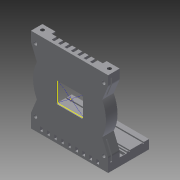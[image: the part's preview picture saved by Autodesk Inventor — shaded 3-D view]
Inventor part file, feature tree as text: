
AUTODESK INVENTOR PART (.ipt)
format: ipt  version: 2013 (Build 170138000, 138)  size: 804,864 bytes
history: native  units: in
note: dims shown in document units (in); Inventor stores cm internally (conversion verified against a paired STEP export)
features: extrude x24, sketch x18, reference x8, projected_geometry x3, thread x2, plane x1
ambient origin geometry x8: Origin, YZ Plane, XZ Plane, XY Plane, X Axis, Y Axis, Z Axis, Center Point
bodies: Solid1 (feature_tree)
feature tree (56):
  extrude  "Extrusion1"  Depth=0.0787in TaperAngle=0.0deg
  extrude  "Extrusion14"  Depth=0.6339in
  extrude  "Extrusion17"  Depth=0.0394in
  extrude  "Extrusion26"  Depth=0.1575in
  extrude  "Extrusion27"  Depth=0.0787in
  extrude  "Extrusion32"  Depth=0.0591in TaperAngle=0.0deg
  extrude  "Extrusion34"  Depth=0.9055in TaperAngle=0.0deg
  extrude  "Extrusion36"  Depth=0.25in
  extrude  "Extrusion37"  Depth=0.25in
  sketch  "Sketch39"  dims[d147=0.1575in d148=0.0591in d149=0.1181in d150=0.0in d151=0.0in]
  extrude  "Extrusion38"  Depth=0.1181in TaperAngle=0.0deg
  extrude  "Extrusion41"  Depth=1.7059in
  extrude  "Extrusion42"  Depth=0.0787in
  extrude  "Extrusion44"  Depth=0.2362in TaperAngle=0.0deg
  extrude  "Extrusion46"  Depth=0.0394in
  extrude  "Extrusion48"  Depth=0.0394in
  extrude  "Extrusion49"  Depth=0.1969in TaperAngle=0.0deg
  extrude  "Extrusion51"  Depth=0.0394in
  extrude  "Extrusion52"  Depth=0.0787in
  extrude  "Extrusion53"  Depth=0.0787in
  extrude  "Extrusion54"  Depth=3.5433in
  plane  "Work Plane1"
  extrude  "Extrusion55"  Depth=0.1969in TaperAngle=0.0deg
  extrude  "Extrusion56"  Depth=0.074in
  extrude  "Extrusion57"  Depth=0.1339in
  extrude  "Extrusion58"  Depth=0.1339in
  thread  "Thread1"  [1 undecoded]
  thread  "Thread2"  [1 undecoded]
  sketch  "Sketch1"  dims[d9=0.3543in d10=0.0in]
  reference  "Reference2"
  reference  "Reference3"
  reference  "Reference4"
  reference  "Reference5"
  sketch  "Sketch26"  dims[d11=0.1181in d12=0.1181in d35=0.3937in d36=0.5906in d37=0.7874in d38=0.9843in d39=0.3937in d40=0.5906in d41=1.1811in d42=1.378in d43=1.5748in d44=1.7717in d94=0.0787in d95=0.0in]
  reference  "Reference6"
  reference  "Reference7"
  sketch  "Sketch27"  dims[d111=0.8189in d112=0.6339in]
  reference  "Reference8"
  reference  "Reference9"
  sketch  "Sketch35"  dims[d113=0.0787in d114=0.0in d115=0.0394in]
  sketch  "Sketch37"  dims[d140=0.0787in d141=0.1575in]
  sketch  "Sketch38"  dims[d142=0.1181in d143=0.0787in d144=0.0in d145=0.0in d146=0.0787in]
  sketch  "Sketch43"  dims[d180=0.2362in d182=0.9055in d183=0.0in]
  sketch  "Sketch49"  dims[d184=0.0591in d185=0.0in d194=0.25in]
  projected_geometry  "Projected Loop6"
  sketch  "Sketch52"  dims[d195=0.3937in d196=0.25in d197=0.0787in]
  projected_geometry  "Projected Loop7"
  sketch  "Sketch54"  dims[d198=0.3937in d199=0.0in d207=0.1181in d208=0.0in]
  sketch  "Sketch55"  dims[d209=1.5307in d211=1.7059in]
  sketch  "Sketch56"  dims[d212=0.0394in d213=0.0in d216=0.0787in]
  sketch  "Sketch57"  dims[d217=1.5748in d218=0.2362in d219=1.3386in d220=0.0in d221=0.0in]
  sketch  "Sketch58"  dims[d233=0.0394in d234=0.0394in]
  sketch  "Sketch59"  dims[d235=0.0787in d236=0.0394in]
  sketch  "Sketch60"  dims[d237=2.7559in d239=0.1969in d240=0.3937in d242=0.3937in d245=0.1969in d246=0.0in]
  projected_geometry  "Projected Loop8"
  sketch  "Sketch61"  dims[d247=0.0394in d248=0.0394in d249=0.0787in d250=0.0787in d251=3.5433in d253=0.2165in d254=0.3937in d256=0.3937in d258=0.1969in d259=0.0in d260=0.074in d275=0.1339in d277=0.1339in d278=1.2598in d279=1.2598in d280=0.1969in d281=0.0in d288=0.0787in d289=0.0in d294=0.1339in d295=0.1181in d296=0.1181in d297=0.0394in d298=0.1969in d299=0.748in d300=0.0in d301=0.0787in d302=0.1181in d303=0.5906in d304=0.3937in d305=0.0in d306=1.5748in d308=0.2165in d309=0.3937in d311=0.3937in d315=0.2756in d320=0.1102in d327=0.5841in d328=0.35in d332=2.1in d333=1.95in d334=0.1102in d335=0.2756in d337=0.2in d339=0.1969in d340=0.1969in d341=0.0394in d342=4.0in d343=2.25in d344=0.0787in d359=1.811in d360=0.2953in d361=0.0in d363=0.2756in d364=0.1102in d366=0.0394in d367=0.0787in d368=0.0394in d369=0.1969in d370=0.0787in d371=0.1575in d372=0.1575in d377=0.1378in d378=0.2681in d379=0.0787in d380=0.1181in d381=3.5433in d383=0.2165in d384=0.3937in d386=0.3937in d388=0.0787in d389=0.2823in d390=0.2823in d391=0.315in d392=0.0in d393=0.1181in d394=0.0in d395=0.0787in d397=0.0787in d398=0.0394in d399=0.1181in d400=0.0in d403=2.2441in d404=0.1969in d405=0.0in d408=0.0039in d410=0.0039in d411=0.0157in d412=0.0276in d413=0.2441in d414=0.0236in d415=0.0433in d416=0.0in d417=1.0651in d418=1.0651in d419=-0.2756in d420=0.0433in d421=0.0in d422=0.0276in d423=0.0276in d424=0.1575in d426=0.0394in d427=0.0in d429=0.0394in d430=0.3937in d432=0.0394in d433=0.0394in d434=0.0394in d435=0.0394in d436=0.0394in d437=0.0in d438=0.1102in d439=0.1575in d440=0.1575in d441=0.1969in d442=0.0in d443=0.3937in d444=0.0in d445=0.3937in d446=0.0in d447=1.5748in]
note: 2 required parameter values undecoded (feature->parameter linkage not recoverable at this tier; creation-order binding heuristic only, values carry confidence <= 0.55)
